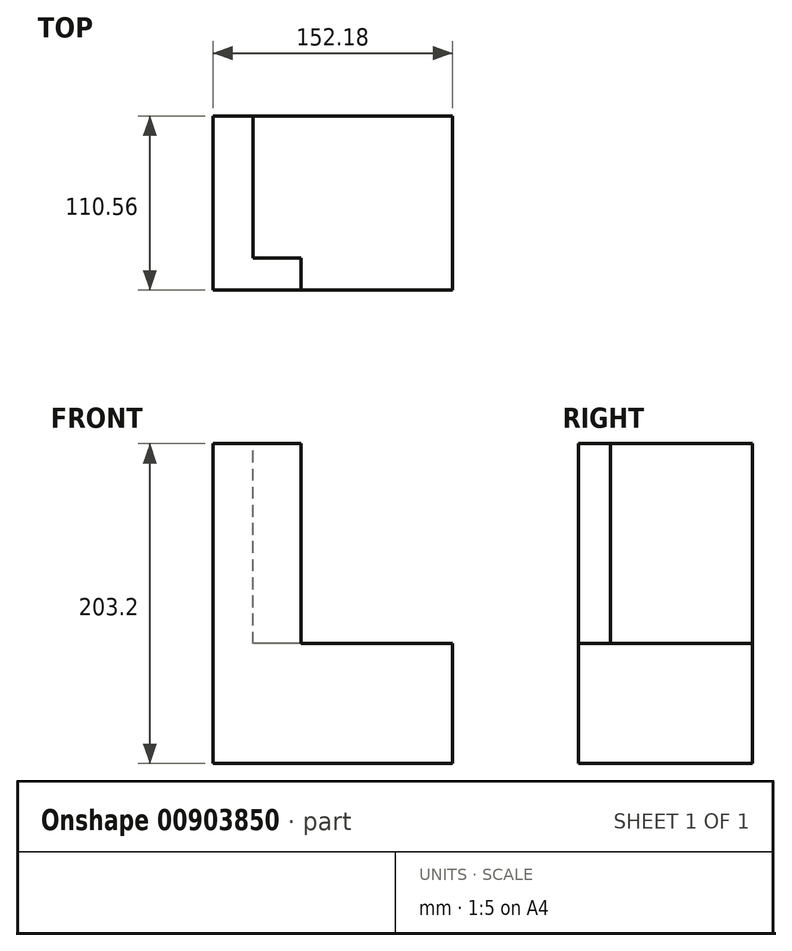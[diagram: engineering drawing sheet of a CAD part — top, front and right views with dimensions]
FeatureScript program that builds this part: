
annotation { "Feature Type Name" : "Feature", "Feature Type Description" : "" }
export const myFeature = defineFeature(function(context is Context, id is Id, definition is map)
    precondition{}
    {
        {
            var Q0;
            Q0=qCreatedBy(makeId("Top.planeOp"),FACE);
            var sketch = newSketch(context, id + "F0", { "sketchPlane" : qUnion([Q0])});
            skLineSegment(sketch, "E0.bottom", {"start": v(76.1, 55.28) * mm, "end": v(-76.1, 55.28) * mm});
            skLineSegment(sketch, "E0.top", {"start": v(76.1, -55.28) * mm, "end": v(-76.1, -55.28) * mm});
            skLineSegment(sketch, "E0.left", {"start": v(76.1, 55.28) * mm, "end": v(76.1, -55.28) * mm});
            skLineSegment(sketch, "E0.right", {"start": v(-76.1, 55.28) * mm, "end": v(-76.1, -55.28) * mm});
            skPoint(sketch, "E0.middle", {"position": v(0, 0) * mm});
            skSolve(sketch);
        }
        {
            var Q0;
            Q0=makeQuery(id+"F0.imprint","IMPRINT",FACE,{"disambiguationData":[TD([[makeQuery(id+"F0.imprint","IMPRINT",EDGE,{"derivedFrom":sQuery(id+"F0.wireOp",EDGE,"E0.bottom")}),1.0]])]});
            extrude(context, id + "F1", {"entities" : qUnion([Q0]), "oppositeDirection" : true, "depth" : 203.2 * mm, "offsetDistance" : 25.4 * mm});
        }
        {
            var Q0;
            Q0=makeQuery(id+"F1.opExtrude","CAP_FACE",FACE,{"disambiguationData":[OSD([sQuery(id+"F0.wireOp",EDGE,"E0.bottom"),sQuery(id+"F0.wireOp",EDGE,"E0.top"),sQuery(id+"F0.wireOp",EDGE,"E0.left"),sQuery(id+"F0.wireOp",EDGE,"E0.right")])],"isStart":true});
            var sketch = newSketch(context, id + "F2", { "sketchPlane" : qUnion([Q0])});
            skLineSegment(sketch, "E1", {"start": v(-76.1, -55.28) * mm, "end": v(-20.17, -55.28) * mm});
            skLineSegment(sketch, "E2", {"start": v(-20.17, -55.28) * mm, "end": v(-20.17, -34.96) * mm});
            skLineSegment(sketch, "E3", {"start": v(-20.17, -34.96) * mm, "end": v(-50.7, -34.96) * mm});
            skLineSegment(sketch, "E4", {"start": v(-50.7, -34.96) * mm, "end": v(-50.7, 55.28) * mm});
            skSolve(sketch);
        }
        {
            var Q0;
            {var subQ2=sQuery(id+"F2.wireOp",EDGE,"E2");Q0=makeQuery(id+"F2.imprint","IMPRINT",FACE,{"disambiguationData":[TD([[makeQuery(id+"F2.imprint","IMPRINT",EDGE,{"derivedFrom":subQ2}),-1.0]])]});}
            extrude(context, id + "F3", {"entities" : qUnion([Q0]), "operationType" : NewBodyOperationType.REMOVE, "oppositeDirection" : true, "depth" : 127 * mm, "offsetDistance" : 25.4 * mm});
        }
    });
